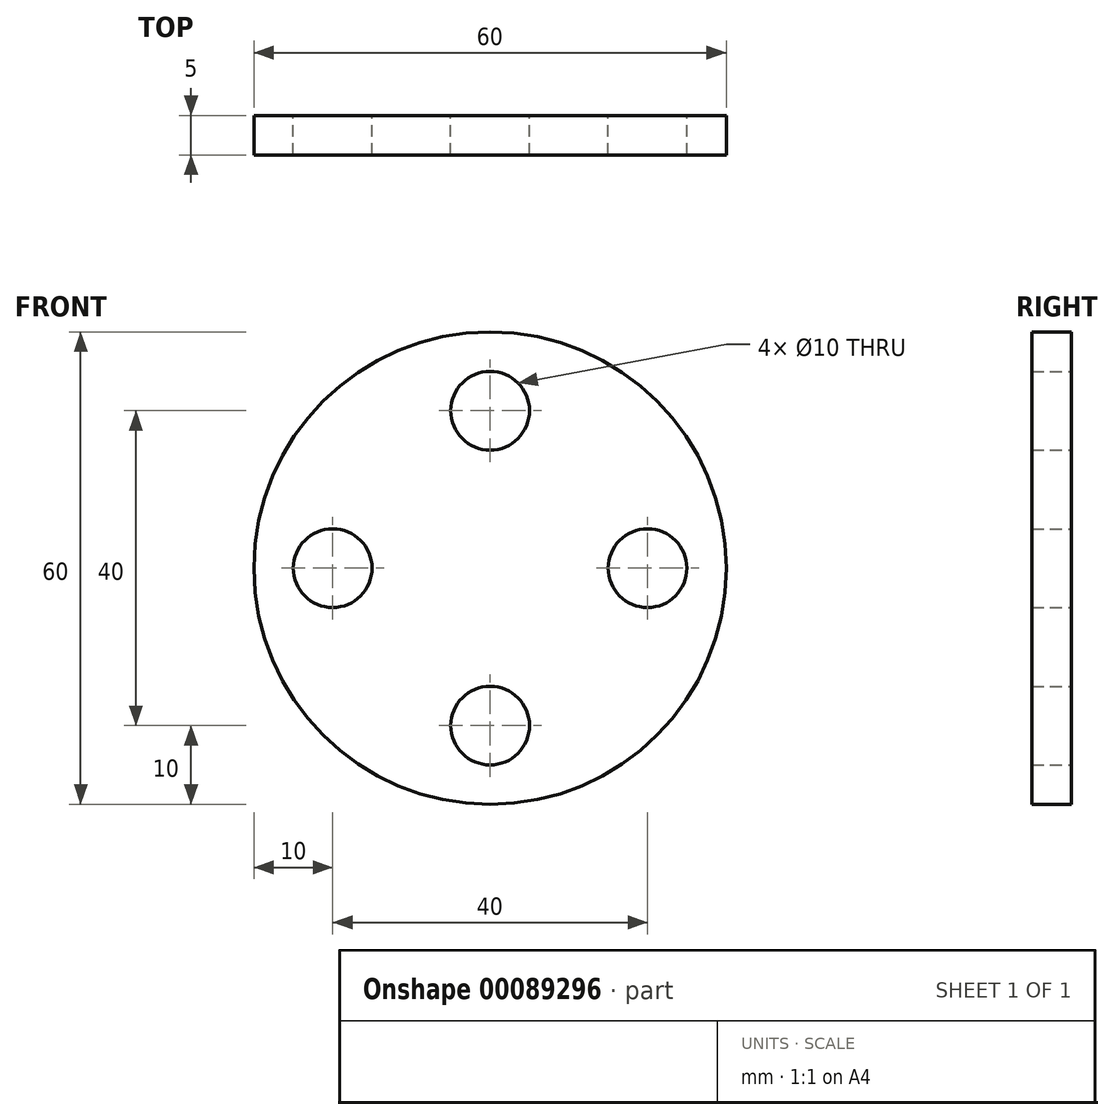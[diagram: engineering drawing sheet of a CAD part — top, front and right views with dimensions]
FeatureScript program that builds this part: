
annotation { "Feature Type Name" : "Feature", "Feature Type Description" : "" }
export const myFeature = defineFeature(function(context is Context, id is Id, definition is map)
    precondition{}
    {
        {
            var Q0;
            Q0=qCreatedBy(makeId("Front.planeOp"),FACE);
            var sketch = newSketch(context, id + "F0", { "sketchPlane" : qUnion([Q0])});
            skCircle(sketch, "E0", {"center": v(0, 0) * mm, "radius": 20 * mm, "construction": true});
            skCircle(sketch, "E1", {"center": v(0, 0) * mm, "radius": 30 * mm});
            skCircle(sketch, "E2", {"center": v(0, 20) * mm, "radius": 5 * mm});
            skCircle(sketch, "E3.1.0", {"center": v(-20, 0) * mm, "radius": 5 * mm});
            skCircle(sketch, "E3.2.0", {"center": v(0, -20) * mm, "radius": 5 * mm});
            skCircle(sketch, "E3.3.0", {"center": v(20, 0) * mm, "radius": 5 * mm});
            skSolve(sketch);
        }
        {
            var Q0;
            Q0 = qSketchRegion(id + "F0", true);
            extrude(context, id + "F1", {"entities" : qUnion([Q0]), "depth" : 5 * mm});
        }
    });
